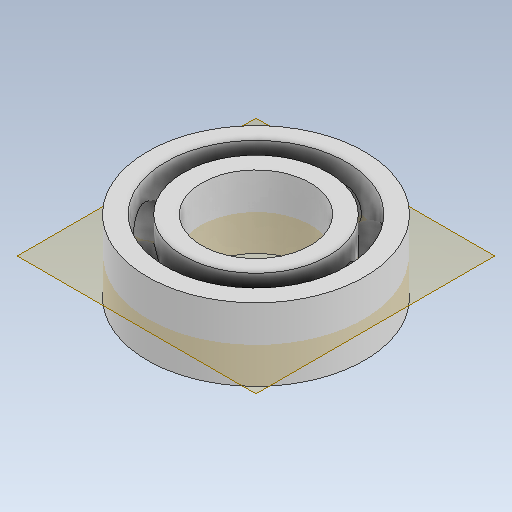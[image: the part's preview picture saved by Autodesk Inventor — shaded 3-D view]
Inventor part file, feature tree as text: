
AUTODESK INVENTOR PART (.ipt)
format: ipt  version: 2020 (Build 240168000, 168)  size: 223,744 bytes
history: native  units: mm
features: other x3, sketch x3, plane x1
ambient origin geometry x8: Origin, YZ Plane, XZ Plane, XY Plane, X Axis, Y Axis, Z Axis, Center Point
bodies: Solid1 (feature_tree)
feature tree (7):
  other  "bearing_3_6_2.ipt"
  other  "Solid1::bearing_3_6_2.ipt"
  other  "TaggingFeature1"
  sketch  "Sketch1"  dims[d0=10.0mm]
  sketch  "Sketch2"
  sketch  "Sketch3"
  plane  "Work Plane1"
